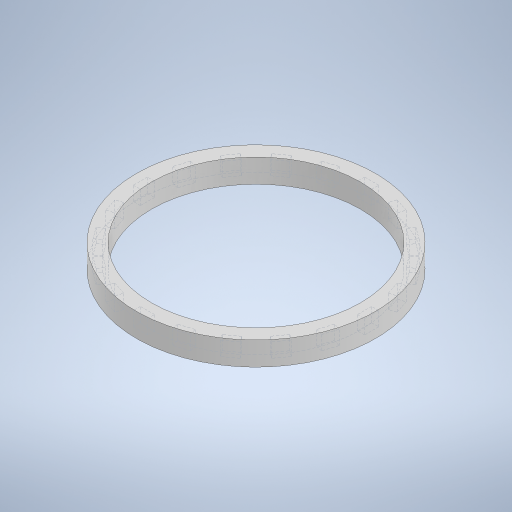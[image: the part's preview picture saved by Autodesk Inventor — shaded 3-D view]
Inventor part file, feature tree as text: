
AUTODESK INVENTOR PART (.ipt)
format: ipt  version: 2023 (Build 270158000, 158)  size: 358,400 bytes
history: native  units: mm
features: extrude x2, sketch x2
ambient origin geometry x8: Origin, YZ Plane, XZ Plane, XY Plane, X Axis, Y Axis, Z Axis, Center Point
bodies: Solid1 (feature_tree)
feature tree (4):
  extrude  "Extrusion1"  Depth=101.6mm
  extrude  "Extrusion2"  Depth=3.0mm
  sketch  "Sketch1"  dims[d0=88.9mm d1=101.6mm]
  sketch  "Sketch2"  dims[d2=10.0mm d3=0.0mm d4=3.0mm d5=6.0mm d6=200.0mm d8=360.0deg d10=6.0mm d11=0.0mm]
